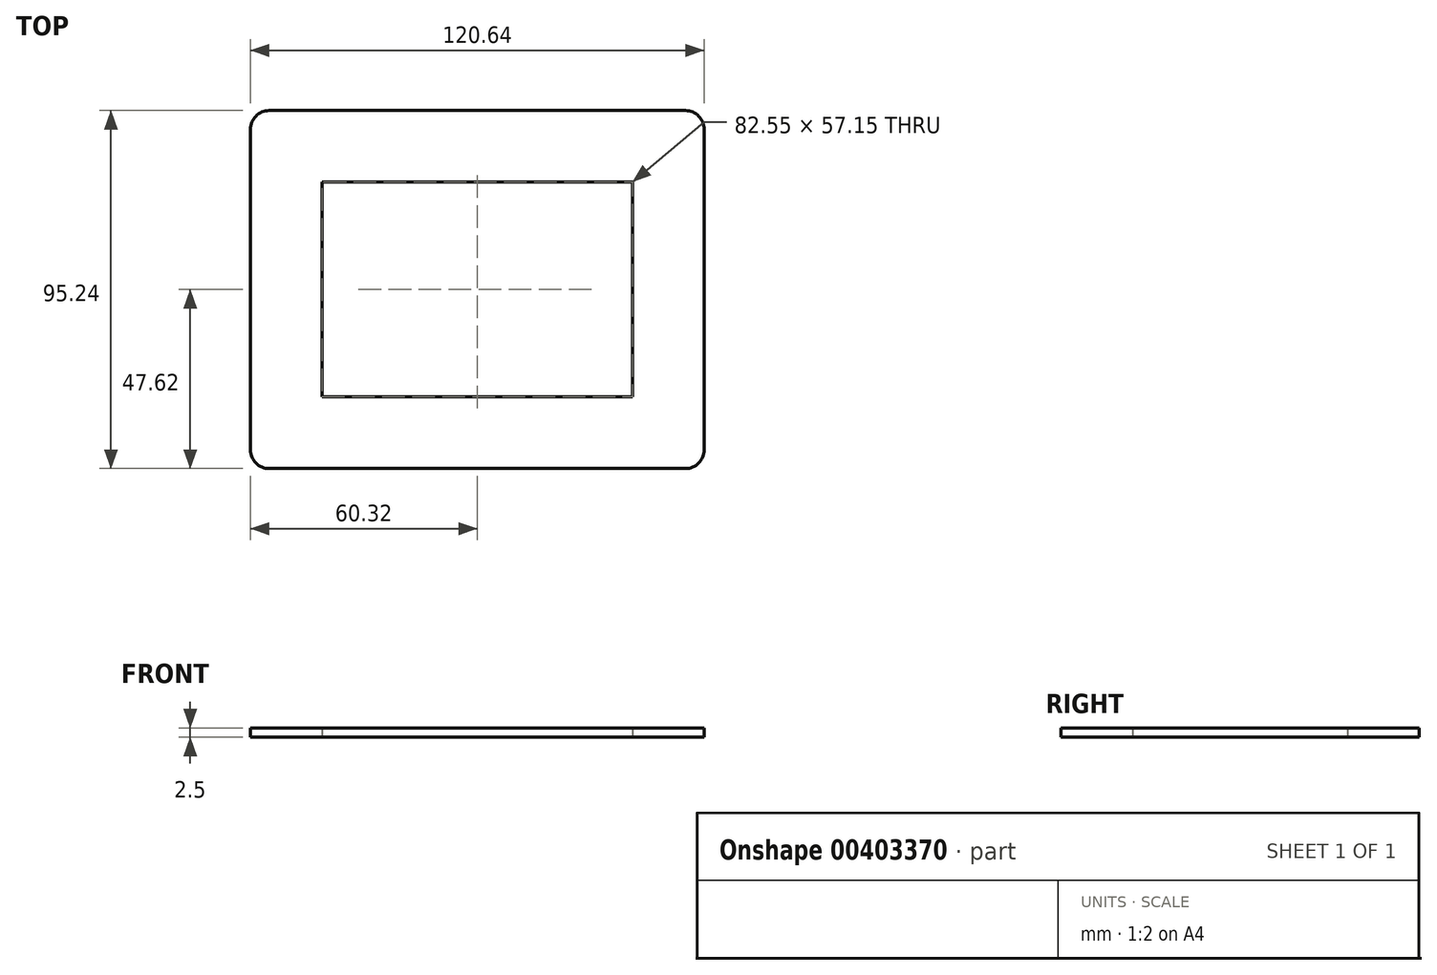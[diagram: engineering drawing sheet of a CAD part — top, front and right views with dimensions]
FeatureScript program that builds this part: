
annotation { "Feature Type Name" : "Feature", "Feature Type Description" : "" }
export const myFeature = defineFeature(function(context is Context, id is Id, definition is map)
    precondition{}
    {
        {
            var Q0;
            Q0=qCreatedBy(makeId("Top.planeOp"),FACE);
            var sketch = newSketch(context, id + "F0", { "sketchPlane" : qUnion([Q0])});
            skLineSegment(sketch, "E0.bottom", {"start": v(60.33, 47.63) * mm, "end": v(-60.33, 47.62) * mm});
            skLineSegment(sketch, "E0.top", {"start": v(60.33, -47.62) * mm, "end": v(-60.33, -47.62) * mm});
            skLineSegment(sketch, "E0.left", {"start": v(60.32, 47.62) * mm, "end": v(60.33, -47.62) * mm});
            skLineSegment(sketch, "E0.right", {"start": v(-60.33, 47.62) * mm, "end": v(-60.33, -47.62) * mm});
            skPoint(sketch, "E0.middle", {"position": v(0, 0) * mm});
            skLineSegment(sketch, "E1.bottom", {"start": v(41.27, 28.58) * mm, "end": v(-41.27, 28.58) * mm});
            skLineSegment(sketch, "E1.top", {"start": v(41.27, -28.58) * mm, "end": v(-41.28, -28.58) * mm});
            skLineSegment(sketch, "E1.left", {"start": v(41.28, 28.58) * mm, "end": v(41.27, -28.58) * mm});
            skLineSegment(sketch, "E1.right", {"start": v(-41.27, 28.58) * mm, "end": v(-41.28, -28.58) * mm});
            skSolve(sketch);
        }
        {
            var Q0;
            Q0=makeQuery(id+"F0.imprint","IMPRINT",FACE,{"disambiguationData":[TD([[makeQuery(id+"F0.imprint","IMPRINT",EDGE,{"derivedFrom":sQuery(id+"F0.wireOp",EDGE,"E0.bottom")}),1.0]])]});
            extrude(context, id + "F1", {"entities" : qUnion([Q0]), "depth" : 2.5 * mm, "offsetDistance" : 25 * mm});
        }
        {
            var Q0;
            Q0=makeQuery(id+"F1.opExtrude","SWEPT_EDGE",EDGE,{"disambiguationData":[OSD([sQuery(id+"F0.wireOp",EDGE,"E0.top"),sQuery(id+"F0.wireOp",EDGE,"E0.right")])]});
            var Q1;
            Q1=makeQuery(id+"F1.opExtrude","SWEPT_EDGE",EDGE,{"disambiguationData":[OSD([sQuery(id+"F0.wireOp",EDGE,"E0.top"),sQuery(id+"F0.wireOp",EDGE,"E0.left")])]});
            var Q2;
            Q2=makeQuery(id+"F1.opExtrude","SWEPT_EDGE",EDGE,{"disambiguationData":[OSD([sQuery(id+"F0.wireOp",EDGE,"E0.bottom"),sQuery(id+"F0.wireOp",EDGE,"E0.right")])]});
            var Q3;
            Q3=makeQuery(id+"F1.opExtrude","SWEPT_EDGE",EDGE,{"disambiguationData":[OSD([sQuery(id+"F0.wireOp",EDGE,"E0.bottom"),sQuery(id+"F0.wireOp",EDGE,"E0.left")])]});
            fillet(context, id + "F2", {"entities" : qUnion([Q0, Q1, Q2, Q3]), "radius" : 5 * mm, "tangentPropagation" : true, "allowEdgeOverflow" : false});
        }
    });
